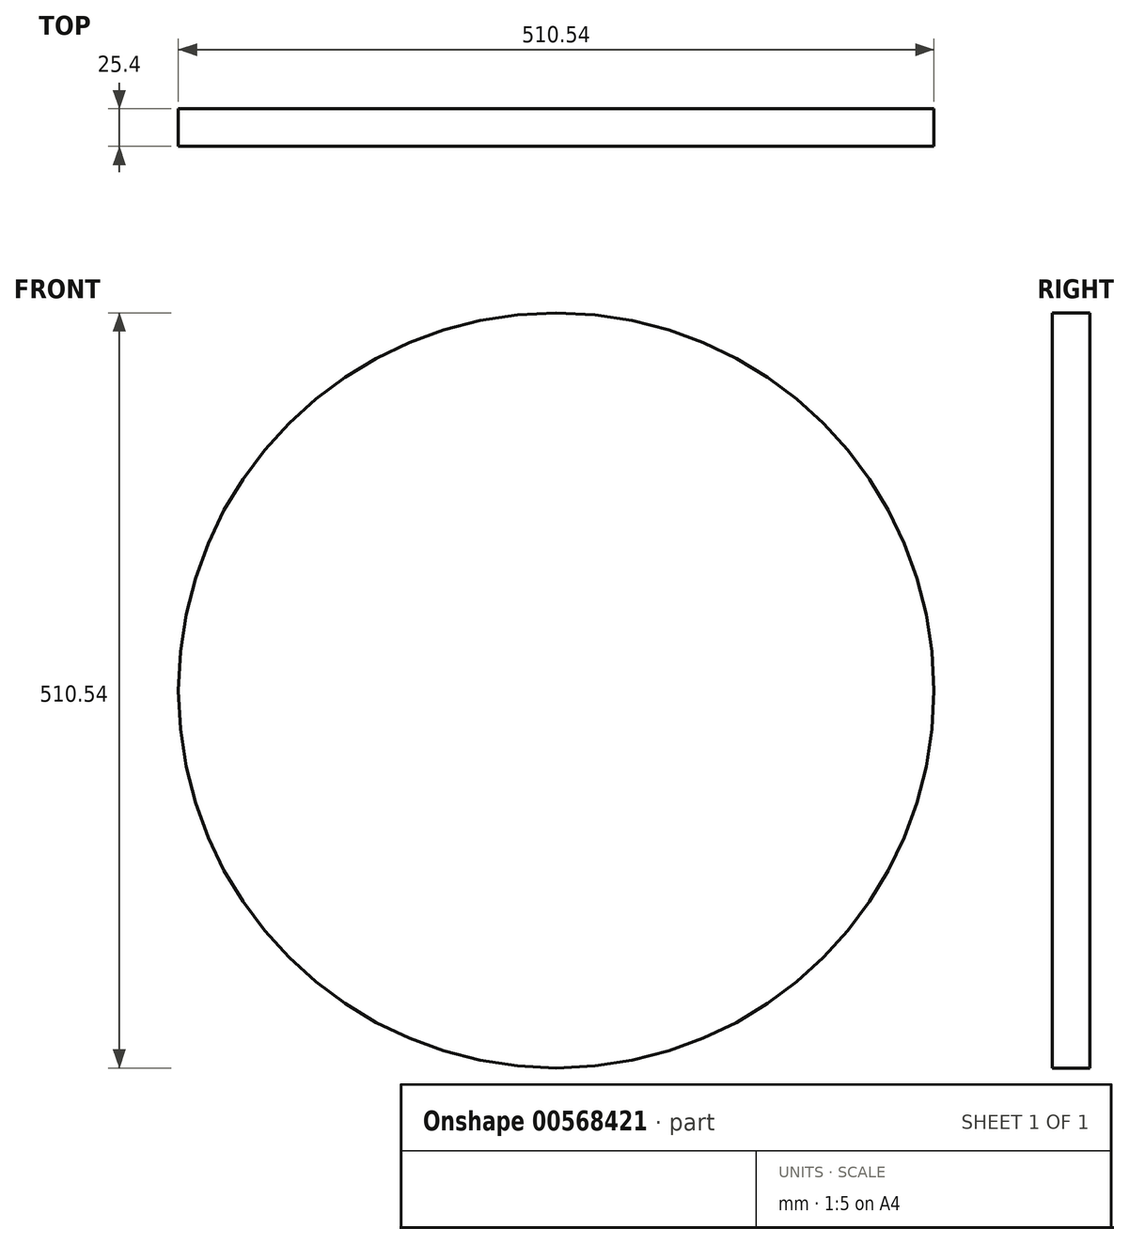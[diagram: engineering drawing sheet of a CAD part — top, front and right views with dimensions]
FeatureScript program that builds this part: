
annotation { "Feature Type Name" : "Feature", "Feature Type Description" : "" }
export const myFeature = defineFeature(function(context is Context, id is Id, definition is map)
    precondition{}
    {
        {
            var Q0;
            Q0=qCreatedBy(makeId("Front.planeOp"),FACE);
            var sketch = newSketch(context, id + "F0", { "sketchPlane" : qUnion([Q0])});
            skCircle(sketch, "E0", {"center": v(2.94, 0) * mm, "radius": 342.9 * mm});
            skCircle(sketch, "E1", {"center": v(0, 0) * mm, "radius": 255.27 * mm});
            skSolve(sketch);
        }
        {
            var Q0;
            Q0=makeQuery(id+"F0.imprint","IMPRINT",FACE,{"disambiguationData":[TD([[makeQuery(id+"F0.imprint","IMPRINT",EDGE,{"derivedFrom":sQuery(id+"F0.wireOp",EDGE,"E1")}),1.0]])]});
            extrude(context, id + "F1", {"entities" : qUnion([Q0]), "depth" : 25.4 * mm, "offsetDistance" : 25.4 * mm});
        }
    });
